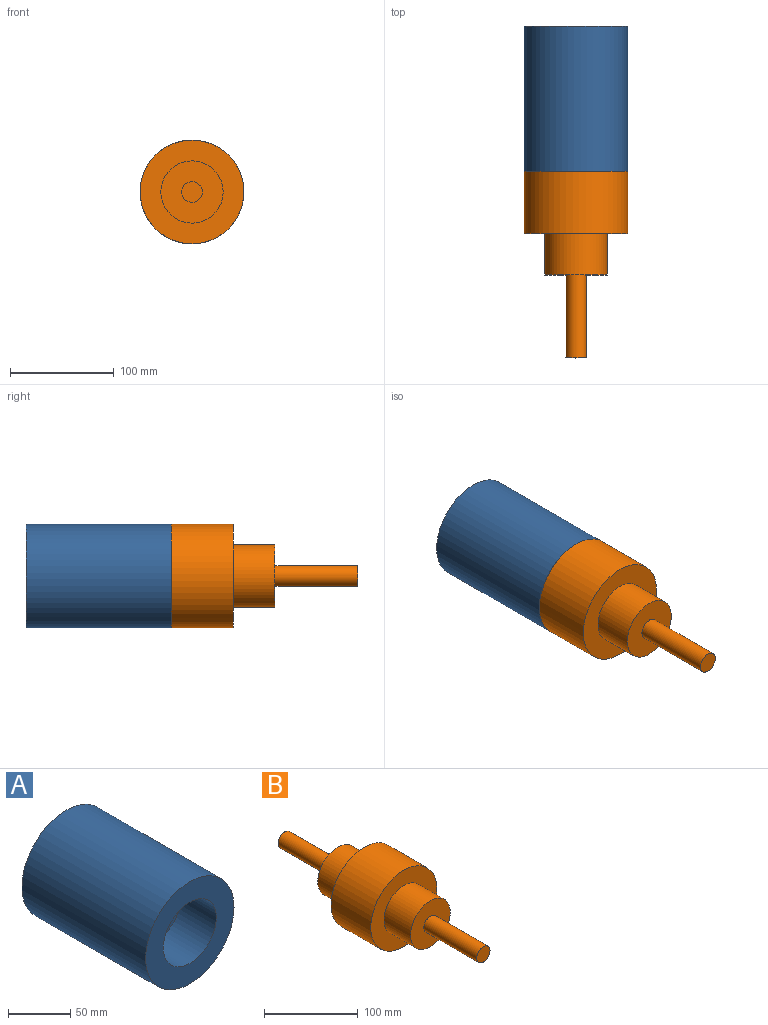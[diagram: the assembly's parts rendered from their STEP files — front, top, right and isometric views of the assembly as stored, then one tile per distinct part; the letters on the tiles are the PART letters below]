
ASSEMBLY  parts=2 mates=1
PART A: 7 faces, bbox 100x140x100 mm
  f0: cylinder r=50mm len=140mm, axis (0,-1,0), area 43982.3mm2, adj f1,f2
  f1: plane 100x100mm, normal (0,1,0), area 7854mm2, adj f0
  f2: plane 100x100mm, normal (0,-1,0), area 5026.5mm2, adj f0,f3
  f3: cylinder r=30mm len=60mm, axis (0,-1,0), area 7539.8mm2, adj f2,f4
  f4: plane 60x60mm, normal (0,-1,0), area 2513.3mm2, adj f3,f6
  f5: plane 20x20mm, normal (0,-1,0), area 314.2mm2, adj f6
  f6: cylinder r=10mm len=80mm, axis (0,-1,0), area 5026.5mm2, adj f4,f5
PART B: 11 faces, bbox 100x300x100 mm
  f0: cylinder r=50mm len=100mm, axis (0,1,0), area 18849.6mm2, adj f1,f2
  f1: plane 100x100mm, normal (0,-1,0), area 5026.5mm2, adj f0,f5
  f2: plane 100x100mm, normal (0,1,0), area 5026.5mm2, adj f0,f3
  f3: cylinder r=30mm len=60mm, axis (0,-1,0), area 7539.8mm2, adj f2,f4
  f4: plane 60x60mm, normal (0,1,0), area 2513.3mm2, adj f3,f9
  f5: cylinder r=30mm len=60mm, axis (0,1,0), area 7539.8mm2, adj f1,f6
  f6: plane 60x60mm, normal (0,-1,0), area 2513.3mm2, adj f5,f7
  f7: cylinder r=10mm len=80mm, axis (0,1,0), area 5026.5mm2, adj f6,f8
  f8: plane 20x20mm, normal (0,-1,0), area 314.2mm2, adj f7
  f9: cylinder r=10mm len=80mm, axis (0,-1,0), area 5026.5mm2, adj f4,f10
  f10: plane 20x20mm, normal (0,1,0), area 314.2mm2, adj f9
PLACE A t=(-32.57,-99.95,22.41)mm
PLACE B t=(-32.57,-129.95,22.41)mm
MATE fastened B.f0 <-> A.f0  axis (0,1,0) through (-32.57,-99.95,22.41)mm
